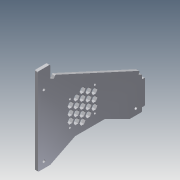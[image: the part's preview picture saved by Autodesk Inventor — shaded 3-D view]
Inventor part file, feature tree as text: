
AUTODESK INVENTOR PART (.ipt)
format: ipt  version: 2014 (Build 180170000, 170)  size: 615,936 bytes
history: native  units: mm
features: extrude x8, sketch x7, fillet x1, pattern_linear x1, projected_geometry x1
ambient origin geometry x8: Origin, YZ Plane, XZ Plane, XY Plane, X Axis, Y Axis, Z Axis, Center Point
bodies: Solid1 (feature_tree)
feature tree (18):
  extrude  "Extrusion1"  Depth=25.0mm
  extrude  "Extrusion2"  Depth=210.0mm
  extrude  "Extrusion3"  Depth=25.0mm
  extrude  "Extrusion4"  Depth=25.0mm
  extrude  "Extrusion5"  Depth=8.1mm TaperAngle=0.0deg
  fillet  "Fillet1"  Radius=8.1mm
  sketch  "Sketch7"  dims[d11=25.0mm d12=3.0mm d13=0.0mm d14=8.1mm]
  extrude  "Extrusion7"  Depth=6.0mm
  pattern_linear  "Rectangular Pattern1"  Spacing1=12.5mm  [1 undecoded]
  extrude  "Extrusion9"  Depth=6.0mm
  extrude  "Extrusion10"  Depth=6.0mm
  sketch  "Sketch2"  dims[d0=175.0mm d1=25.0mm]
  sketch  "Sketch3"  dims[d3=65.0mm d4=210.0mm]
  sketch  "Sketch4"  dims[d5=6.0mm d6=0.0mm d8=25.0mm]
  sketch  "Sketch6"  dims[d9=25.0mm d10=50.0mm]
  sketch  "Sketch8"  dims[d15=8.1mm d16=6.0mm]
  sketch  "Sketch9"  dims[d17=6.0mm d18=0.0mm d19=12.5mm d20=37.5mm d21=12.5mm d22=12.5mm d23=5.4mm d24=6.0mm d25=0.0mm d26=2.0mm d27=185.0mm d28=85.0mm d33=8.1mm d34=6.0mm d35=0.0mm d36=8.1mm d38=6.0mm d39=50.0mm d41=60.0mm d42=15.0mm d43=60.0mm d44=4.3mm d48=3.5mm d49=12.0mm d50=6.928203mm d51=72.712mm d52=66.0mm d53=10.0mm d54=0.0mm d55=40.0mm d57=24.0mm d58=50.0mm d60=13.856mm d63=6.0mm d64=0.0mm d65=6.0mm d66=0.0mm]
  projected_geometry  "Projected Loop1"
note: 1 required parameter value undecoded (feature->parameter linkage not recoverable at this tier; creation-order binding heuristic only, values carry confidence <= 0.55)
